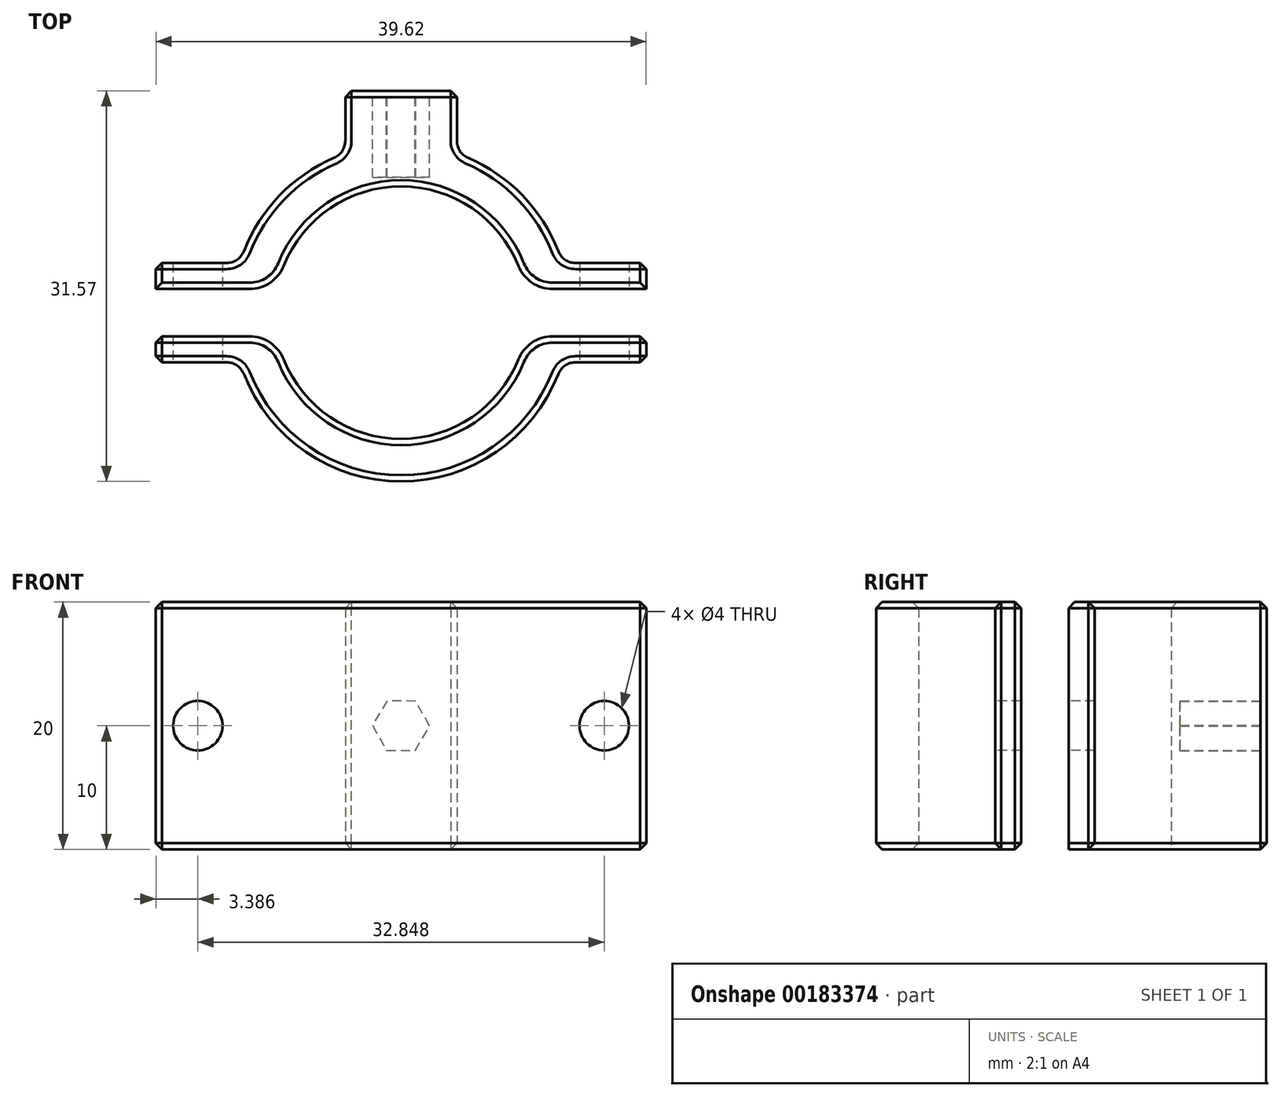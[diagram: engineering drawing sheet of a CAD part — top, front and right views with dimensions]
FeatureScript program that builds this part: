
annotation { "Feature Type Name" : "Feature", "Feature Type Description" : "" }
export const myFeature = defineFeature(function(context is Context, id is Id, definition is map)
    precondition{}
    {
        {
            var Q0;
            Q0=qCreatedBy(makeId("Top.planeOp"),FACE);
            var sketch = newSketch(context, id + "F15", { "sketchPlane" : qUnion([Q0])});
            skCircle(sketch, "E0", {"center": v(0, 0) * mm, "radius": 13.64 * mm});
            skCircle(sketch, "E1", {"center": v(0, 0) * mm, "radius": 10 * mm});
            skSolve(sketch);
        }
        {
            var Q0;
            Q0=makeQuery(id+"F15.imprint","IMPRINT",FACE,{"disambiguationData":[TD([[makeQuery(id+"F15.imprint","IMPRINT",EDGE,{"derivedFrom":sQuery(id+"F15.wireOp",EDGE,"d60e790e-70cd-4cc0-8c0c-df4997ba0fd5")}),-1.0]])]});
            var Q1;
            Q1=makeQuery(id+"F15.imprint","IMPRINT",FACE,{"disambiguationData":[TD([[makeQuery(id+"F15.imprint","IMPRINT",EDGE,{"derivedFrom":sQuery(id+"F15.wireOp",EDGE,"E0")}),1.0]])]});
            extrude(context, id + "F16", {"entities" : qUnion([Q0, Q1]), "depth" : 20 * mm});
        }
        {
            var Q0;
            Q0=qCreatedBy(makeId("Top.planeOp"),FACE);
            var sketch = newSketch(context, id + "F0", { "sketchPlane" : qUnion([Q0])});
            skLineSegment(sketch, "E2.bottom", {"start": v(19.81, 4.02) * mm, "end": v(-19.81, 4.02) * mm});
            skLineSegment(sketch, "E2.top", {"start": v(19.81, -4.02) * mm, "end": v(-19.81, -4.02) * mm});
            skLineSegment(sketch, "E2.left", {"start": v(19.81, 4.02) * mm, "end": v(19.81, -4.02) * mm});
            skLineSegment(sketch, "E2.right", {"start": v(-19.81, 4.02) * mm, "end": v(-19.81, -4.02) * mm});
            skPoint(sketch, "E2.middle", {"position": v(0, 0) * mm});
            skSolve(sketch);
        }
        {
            var Q0;
            Q0=qCreatedBy(makeId("Top.planeOp"),FACE);
            var sketch = newSketch(context, id + "F1", { "sketchPlane" : qUnion([Q0])});
            skLineSegment(sketch, "E3.bottom", {"start": v(19.81, 1.92) * mm, "end": v(-19.81, 1.92) * mm});
            skLineSegment(sketch, "E3.top", {"start": v(19.81, -1.92) * mm, "end": v(-19.81, -1.92) * mm});
            skLineSegment(sketch, "E3.left", {"start": v(19.81, 1.92) * mm, "end": v(19.81, -1.92) * mm});
            skLineSegment(sketch, "E3.right", {"start": v(-19.81, 1.92) * mm, "end": v(-19.81, -1.92) * mm});
            skPoint(sketch, "E3.middle", {"position": v(0, 0) * mm});
            skSolve(sketch);
        }
        {
            var Q0;
            Q0=makeQuery(id+"F0.imprint","IMPRINT",FACE,{"disambiguationData":[TD([[makeQuery(id+"F0.imprint","IMPRINT",EDGE,{"derivedFrom":sQuery(id+"F0.wireOp",EDGE,"E2.bottom")}),1.0]])]});
            extrude(context, id + "F17", {"entities" : qUnion([Q0]), "operationType" : NewBodyOperationType.ADD, "depth" : 20 * mm});
        }
        {
            var Q0;
            Q0=makeQuery(id+"F1.imprint","IMPRINT",FACE,{"disambiguationData":[TD([[makeQuery(id+"F1.imprint","IMPRINT",EDGE,{"derivedFrom":sQuery(id+"F1.wireOp",EDGE,"E3.bottom")}),1.0]])]});
            extrude(context, id + "F2", {"entities" : qUnion([Q0]), "operationType" : NewBodyOperationType.REMOVE, "depth" : 25 * mm});
        }
        {
            var Q0;
            Q0=qCreatedBy(makeId("Top.planeOp"),FACE);
            var sketch = newSketch(context, id + "F3", { "sketchPlane" : qUnion([Q0])});
            skCircle(sketch, "E4", {"center": v(0, 0) * mm, "radius": 10.2 * mm});
            skSolve(sketch);
        }
        {
            var Q0;
            Q0=makeQuery(id+"F3.imprint","IMPRINT",FACE,{"disambiguationData":[TD([[makeQuery(id+"F3.imprint","IMPRINT",EDGE,{"derivedFrom":sQuery(id+"F3.wireOp",EDGE,"E4")}),1.0]])]});
            extrude(context, id + "F18", {"entities" : qUnion([Q0]), "operationType" : NewBodyOperationType.REMOVE, "depth" : 25 * mm});
        }
        {
            var Q0;
            {var subQ1=sQuery(id+"F0.wireOp",EDGE,"E2.left");var subQ2=sQuery(id+"F0.wireOp",EDGE,"E2.top");Q0=makeQuery(id+"F17.boolean.opBoolean","SPLIT",FACE,{"disambiguationData":[TD([makeQuery(id+"F17.opExtrude","SWEPT_FACE",FACE,{"disambiguationData":[OSD([subQ1])]})])],"derivedFrom":makeQuery(id+"F17.opExtrude","SWEPT_FACE",FACE,{"disambiguationData":[OSD([subQ2])]})});}
            var sketch = newSketch(context, id + "F4", { "sketchPlane" : qUnion([Q0])});
            skLineSegment(sketch, "E5", {"start": v(19.81, 10) * mm, "end": v(13.03, 10) * mm, "construction": true});
            skLineSegment(sketch, "E6", {"start": v(16.42, 0) * mm, "end": v(16.42, 20) * mm, "construction": true});
            skPoint(sketch, "E7", {"position": v(16.42, 10) * mm});
            skSolve(sketch);
        }
        {
            var Q0;
            {var subQ0=sQuery(id+"F0.wireOp",EDGE,"E2.right");var subQ2=sQuery(id+"F0.wireOp",EDGE,"E2.top");Q0=makeQuery(id+"F17.boolean.opBoolean","SPLIT",FACE,{"disambiguationData":[TD([makeQuery(id+"F17.opExtrude","SWEPT_FACE",FACE,{"disambiguationData":[OSD([subQ0])]})])],"derivedFrom":makeQuery(id+"F17.opExtrude","SWEPT_FACE",FACE,{"disambiguationData":[OSD([subQ2])]})});}
            var sketch = newSketch(context, id + "F5", { "sketchPlane" : qUnion([Q0])});
            skLineSegment(sketch, "E8", {"start": v(-19.81, 10) * mm, "end": v(-13.03, 10) * mm, "construction": true});
            skLineSegment(sketch, "E9", {"start": v(-16.42, 0) * mm, "end": v(-16.42, 20) * mm, "construction": true});
            skPoint(sketch, "E10", {"position": v(-16.42, 10) * mm});
            skSolve(sketch);
        }
        {
            var Q0;
            Q0=sQuery(id+"F4.wireOp",VERTEX,"E7");
            var Q1;
            Q1=makeQuery(id+"F2.boolean.opBoolean","SPLIT",BODY,{"disambiguationData":[OD(0.0)],"derivedFrom":makeQuery(id+"F16.opExtrude","SWEPT_BODY",BODY,{"disambiguationData":[OSD([sQuery(id+"F15.wireOp",EDGE,"E0"),sQuery(id+"F15.wireOp",EDGE,"E1")])]})});
            var Q2;
            Q2=makeQuery(id+"F2.boolean.opBoolean","SPLIT",BODY,{"disambiguationData":[OD(1.0)],"derivedFrom":makeQuery(id+"F16.opExtrude","SWEPT_BODY",BODY,{"disambiguationData":[OSD([sQuery(id+"F15.wireOp",EDGE,"E0"),sQuery(id+"F15.wireOp",EDGE,"E1")])]})});
            hole(context, id + "F6", {"style" : HoleStyle.SIMPLE, "endStyle" : HoleEndStyle.THROUGH, "holeDiameter" : 4 * mm, "locations" : qUnion([Q0]), "scope" : qUnion([Q1, Q2]), "isTappedThrough" : true});
        }
        {
            var Q0;
            Q0=sQuery(id+"F5.wireOp",VERTEX,"E10");
            var Q1;
            Q1=makeQuery(id+"F2.boolean.opBoolean","SPLIT",BODY,{"disambiguationData":[OD(0.0)],"derivedFrom":makeQuery(id+"F16.opExtrude","SWEPT_BODY",BODY,{"disambiguationData":[OSD([sQuery(id+"F15.wireOp",EDGE,"E0"),sQuery(id+"F15.wireOp",EDGE,"E1")])]})});
            var Q2;
            Q2=makeQuery(id+"F2.boolean.opBoolean","SPLIT",BODY,{"disambiguationData":[OD(1.0)],"derivedFrom":makeQuery(id+"F16.opExtrude","SWEPT_BODY",BODY,{"disambiguationData":[OSD([sQuery(id+"F15.wireOp",EDGE,"E0"),sQuery(id+"F15.wireOp",EDGE,"E1")])]})});
            hole(context, id + "F7", {"style" : HoleStyle.SIMPLE, "endStyle" : HoleEndStyle.THROUGH, "holeDiameter" : 4 * mm, "locations" : qUnion([Q0]), "scope" : qUnion([Q1, Q2]), "isTappedThrough" : true});
        }
        {
            var Q0;
            Q0=qCreatedBy(makeId("Top.planeOp"),FACE);
            var sketch = newSketch(context, id + "F8", { "sketchPlane" : qUnion([Q0])});
            skLineSegment(sketch, "E11.bottom", {"start": v(4.5, 17.93) * mm, "end": v(-4.5, 17.93) * mm});
            skLineSegment(sketch, "E11.top", {"start": v(4.5, 10.7) * mm, "end": v(-4.5, 10.7) * mm});
            skLineSegment(sketch, "E11.left", {"start": v(4.5, 17.93) * mm, "end": v(4.5, 10.7) * mm});
            skLineSegment(sketch, "E11.right", {"start": v(-4.5, 17.93) * mm, "end": v(-4.5, 10.7) * mm});
            skPoint(sketch, "E11.middle", {"position": v(0, 14.31) * mm});
            skSolve(sketch);
        }
        {
            var Q0;
            Q0=makeQuery(id+"F8.imprint","IMPRINT",FACE,{"disambiguationData":[TD([[makeQuery(id+"F8.imprint","IMPRINT",EDGE,{"derivedFrom":sQuery(id+"F8.wireOp",EDGE,"E11.bottom")}),1.0]])]});
            extrude(context, id + "F9", {"entities" : qUnion([Q0]), "operationType" : NewBodyOperationType.ADD, "depth" : 20 * mm});
        }
        {
            var Q0;
            Q0=makeQuery(id+"F9.opExtrude","SWEPT_FACE",FACE,{"disambiguationData":[OSD([sQuery(id+"F8.wireOp",EDGE,"E11.bottom")])]});
            var sketch = newSketch(context, id + "F10", { "sketchPlane" : qUnion([Q0])});
            skLineSegment(sketch, "E12", {"start": v(0, 0) * mm, "end": v(0, 20) * mm, "construction": true});
            skLineSegment(sketch, "E13", {"start": v(4.5, 10) * mm, "end": v(-4.5, 10) * mm, "construction": true});
            skCircle(sketch, "E14", {"center": v(0, 10) * mm, "radius": 2 * mm});
            skCircle(sketch, "E15.cCircle", {"center": v(0, 10) * mm, "radius": 2 * mm, "construction": true});
            skLineSegment(sketch, "E15.0", {"start": v(2.3, 10.03) * mm, "end": v(1.18, 8.01) * mm});
            skLineSegment(sketch, "E15.1", {"start": v(1.18, 8.01) * mm, "end": v(-1.13, 7.99) * mm});
            skLineSegment(sketch, "E15.2", {"start": v(-1.13, 7.99) * mm, "end": v(-2.3, 9.97) * mm});
            skLineSegment(sketch, "E15.3", {"start": v(-2.3, 9.97) * mm, "end": v(-1.18, 11.99) * mm});
            skLineSegment(sketch, "E15.4", {"start": v(-1.18, 11.99) * mm, "end": v(1.13, 12.01) * mm});
            skLineSegment(sketch, "E15.5", {"start": v(1.13, 12.01) * mm, "end": v(2.3, 10.03) * mm});
            skPoint(sketch, "E15.0.midPoint", {"position": v(1.74, 9.02) * mm});
            skSolve(sketch);
        }
        {
            var Q0;
            Q0=makeQuery(id+"F17.boolean.opBoolean","INTERSECT",EDGE,{"disambiguationData":[OD(0.0)],"derivedFrom":[makeQuery(id+"F16.opExtrude","SWEPT_FACE",FACE,{"disambiguationData":[OSD([sQuery(id+"F15.wireOp",EDGE,"E0")])]}),makeQuery(id+"F17.opExtrude","SWEPT_FACE",FACE,{"disambiguationData":[OSD([sQuery(id+"F0.wireOp",EDGE,"E2.bottom")])]})]});
            var Q1;
            Q1=makeQuery(id+"F17.boolean.opBoolean","INTERSECT",EDGE,{"disambiguationData":[OD(1.0)],"derivedFrom":[makeQuery(id+"F16.opExtrude","SWEPT_FACE",FACE,{"disambiguationData":[OSD([sQuery(id+"F15.wireOp",EDGE,"E0")])]}),makeQuery(id+"F17.opExtrude","SWEPT_FACE",FACE,{"disambiguationData":[OSD([sQuery(id+"F0.wireOp",EDGE,"E2.bottom")])]})]});
            var Q2;
            {var subQ3=sQuery(id+"F0.wireOp",EDGE,"E2.bottom");var subQ5=sQuery(id+"F15.wireOp",EDGE,"E0");Q2=makeQuery(id+"F9.boolean.opBoolean","INTERSECT",EDGE,{"derivedFrom":[makeQuery(id+"F17.boolean.opBoolean","SPLIT",FACE,{"disambiguationData":[TD([makeQuery(id+"F17.opExtrude","SWEPT_FACE",FACE,{"disambiguationData":[OSD([subQ3])]})])],"derivedFrom":makeQuery(id+"F16.opExtrude","SWEPT_FACE",FACE,{"disambiguationData":[OSD([subQ5])]})}),makeQuery(id+"F9.opExtrude","SWEPT_FACE",FACE,{"disambiguationData":[OSD([sQuery(id+"F8.wireOp",EDGE,"E11.right")])]})]});}
            var Q3;
            {var subQ3=sQuery(id+"F0.wireOp",EDGE,"E2.bottom");var subQ5=sQuery(id+"F15.wireOp",EDGE,"E0");Q3=makeQuery(id+"F9.boolean.opBoolean","INTERSECT",EDGE,{"derivedFrom":[makeQuery(id+"F17.boolean.opBoolean","SPLIT",FACE,{"disambiguationData":[TD([makeQuery(id+"F17.opExtrude","SWEPT_FACE",FACE,{"disambiguationData":[OSD([subQ3])]})])],"derivedFrom":makeQuery(id+"F16.opExtrude","SWEPT_FACE",FACE,{"disambiguationData":[OSD([subQ5])]})}),makeQuery(id+"F9.opExtrude","SWEPT_FACE",FACE,{"disambiguationData":[OSD([sQuery(id+"F8.wireOp",EDGE,"E11.left")])]})]});}
            var Q4;
            Q4=makeQuery(id+"F17.boolean.opBoolean","INTERSECT",EDGE,{"disambiguationData":[OD(1.0)],"derivedFrom":[makeQuery(id+"F16.opExtrude","SWEPT_FACE",FACE,{"disambiguationData":[OSD([sQuery(id+"F15.wireOp",EDGE,"E0")])]}),makeQuery(id+"F17.opExtrude","SWEPT_FACE",FACE,{"disambiguationData":[OSD([sQuery(id+"F0.wireOp",EDGE,"E2.top")])]})]});
            var Q5;
            Q5=makeQuery(id+"F17.boolean.opBoolean","INTERSECT",EDGE,{"disambiguationData":[OD(0.0)],"derivedFrom":[makeQuery(id+"F16.opExtrude","SWEPT_FACE",FACE,{"disambiguationData":[OSD([sQuery(id+"F15.wireOp",EDGE,"E0")])]}),makeQuery(id+"F17.opExtrude","SWEPT_FACE",FACE,{"disambiguationData":[OSD([sQuery(id+"F0.wireOp",EDGE,"E2.top")])]})]});
            fillet(context, id + "F11", {"entities" : qUnion([Q0, Q1, Q2, Q3, Q4, Q5]), "radius" : 1.5 * mm, "tangentPropagation" : true, "allowEdgeOverflow" : false});
        }
        {
            var Q0;
            Q0=makeQuery(id+"F18.boolean.opBoolean","INTERSECT",EDGE,{"disambiguationData":[OD(1.0)],"derivedFrom":[makeQuery(id+"F2.boolean.opBoolean","COPY",FACE,{"derivedFrom":makeQuery(id+"F2.opExtrude","SWEPT_FACE",FACE,{"disambiguationData":[OSD([sQuery(id+"F1.wireOp",EDGE,"E3.bottom")])]})}),makeQuery(id+"F18.opExtrude","SWEPT_FACE",FACE,{"disambiguationData":[OSD([sQuery(id+"F3.wireOp",EDGE,"E4")])]})]});
            var Q1;
            Q1=makeQuery(id+"F18.boolean.opBoolean","INTERSECT",EDGE,{"disambiguationData":[OD(0.0)],"derivedFrom":[makeQuery(id+"F2.boolean.opBoolean","COPY",FACE,{"derivedFrom":makeQuery(id+"F2.opExtrude","SWEPT_FACE",FACE,{"disambiguationData":[OSD([sQuery(id+"F1.wireOp",EDGE,"E3.bottom")])]})}),makeQuery(id+"F18.opExtrude","SWEPT_FACE",FACE,{"disambiguationData":[OSD([sQuery(id+"F3.wireOp",EDGE,"E4")])]})]});
            var Q2;
            Q2=makeQuery(id+"F18.boolean.opBoolean","INTERSECT",EDGE,{"disambiguationData":[OD(1.0)],"derivedFrom":[makeQuery(id+"F2.boolean.opBoolean","COPY",FACE,{"derivedFrom":makeQuery(id+"F2.opExtrude","SWEPT_FACE",FACE,{"disambiguationData":[OSD([sQuery(id+"F1.wireOp",EDGE,"E3.top")])]})}),makeQuery(id+"F18.opExtrude","SWEPT_FACE",FACE,{"disambiguationData":[OSD([sQuery(id+"F3.wireOp",EDGE,"E4")])]})]});
            var Q3;
            Q3=makeQuery(id+"F18.boolean.opBoolean","INTERSECT",EDGE,{"disambiguationData":[OD(0.0)],"derivedFrom":[makeQuery(id+"F2.boolean.opBoolean","COPY",FACE,{"derivedFrom":makeQuery(id+"F2.opExtrude","SWEPT_FACE",FACE,{"disambiguationData":[OSD([sQuery(id+"F1.wireOp",EDGE,"E3.top")])]})}),makeQuery(id+"F18.opExtrude","SWEPT_FACE",FACE,{"disambiguationData":[OSD([sQuery(id+"F3.wireOp",EDGE,"E4")])]})]});
            fillet(context, id + "F12", {"entities" : qUnion([Q0, Q1, Q2, Q3]), "radius" : 3 * mm, "tangentPropagation" : true, "allowEdgeOverflow" : false});
        }
        {
            var Q0;
            {var subQ0=sQuery(id+"F15.wireOp",EDGE,"E0");var subQ1=sQuery(id+"F0.wireOp",EDGE,"E2.bottom");Q0=makeQuery(id+"F17.boolean.opBoolean","SPLIT",EDGE,{"disambiguationData":[TD([makeQuery(id+"F17.opExtrude","SWEPT_FACE",FACE,{"disambiguationData":[OSD([subQ1])]})])],"derivedFrom":makeQuery(id+"F16.opExtrude","CAP_EDGE",EDGE,{"disambiguationData":[OSD([subQ0])],"isStart":false})});}
            var Q1;
            {var subQ0=sQuery(id+"F15.wireOp",EDGE,"E0");var subQ1=sQuery(id+"F0.wireOp",EDGE,"E2.bottom");Q1=makeQuery(id+"F17.boolean.opBoolean","SPLIT",EDGE,{"disambiguationData":[TD([makeQuery(id+"F17.opExtrude","SWEPT_FACE",FACE,{"disambiguationData":[OSD([subQ1])]})])],"derivedFrom":makeQuery(id+"F16.opExtrude","CAP_EDGE",EDGE,{"disambiguationData":[OSD([subQ0])],"isStart":true})});}
            var Q2;
            {var subQ0=sQuery(id+"F0.wireOp",EDGE,"E2.right");var subQ1=sQuery(id+"F0.wireOp",EDGE,"E2.bottom");Q2=makeQuery(id+"F17.boolean.opBoolean","SPLIT",EDGE,{"disambiguationData":[TD([makeQuery(id+"F17.opExtrude","SWEPT_FACE",FACE,{"disambiguationData":[OSD([subQ0])]})])],"derivedFrom":makeQuery(id+"F17.opExtrude","CAP_EDGE",EDGE,{"disambiguationData":[OSD([subQ1])],"isStart":false})});}
            var Q3;
            Q3=makeQuery(id+"F17.opExtrude","SWEPT_EDGE",EDGE,{"disambiguationData":[OSD([sQuery(id+"F0.wireOp",EDGE,"E2.bottom"),sQuery(id+"F0.wireOp",EDGE,"E2.right")])]});
            var Q4;
            {var subQ0=sQuery(id+"F0.wireOp",EDGE,"E2.right");var subQ1=sQuery(id+"F0.wireOp",EDGE,"E2.bottom");Q4=makeQuery(id+"F17.boolean.opBoolean","SPLIT",EDGE,{"disambiguationData":[TD([makeQuery(id+"F17.opExtrude","SWEPT_FACE",FACE,{"disambiguationData":[OSD([subQ0])]})])],"derivedFrom":makeQuery(id+"F17.opExtrude","CAP_EDGE",EDGE,{"disambiguationData":[OSD([subQ1])],"isStart":true})});}
            var Q5;
            {var subQ0=sQuery(id+"F0.wireOp",EDGE,"E2.left");var subQ1=sQuery(id+"F0.wireOp",EDGE,"E2.bottom");Q5=makeQuery(id+"F17.boolean.opBoolean","SPLIT",EDGE,{"disambiguationData":[TD([makeQuery(id+"F17.opExtrude","SWEPT_FACE",FACE,{"disambiguationData":[OSD([subQ0])]})])],"derivedFrom":makeQuery(id+"F17.opExtrude","CAP_EDGE",EDGE,{"disambiguationData":[OSD([subQ1])],"isStart":false})});}
            var Q6;
            Q6=makeQuery(id+"F17.opExtrude","SWEPT_EDGE",EDGE,{"disambiguationData":[OSD([sQuery(id+"F0.wireOp",EDGE,"E2.bottom"),sQuery(id+"F0.wireOp",EDGE,"E2.left")])]});
            var Q7;
            {var subQ0=sQuery(id+"F0.wireOp",EDGE,"E2.left");var subQ1=sQuery(id+"F0.wireOp",EDGE,"E2.bottom");Q7=makeQuery(id+"F17.boolean.opBoolean","SPLIT",EDGE,{"disambiguationData":[TD([makeQuery(id+"F17.opExtrude","SWEPT_FACE",FACE,{"disambiguationData":[OSD([subQ0])]})])],"derivedFrom":makeQuery(id+"F17.opExtrude","CAP_EDGE",EDGE,{"disambiguationData":[OSD([subQ1])],"isStart":true})});}
            var Q8;
            Q8=makeQuery(id+"F9.opExtrude","CAP_EDGE",EDGE,{"disambiguationData":[OSD([sQuery(id+"F8.wireOp",EDGE,"E11.bottom")])],"isStart":false});
            var Q9;
            Q9=makeQuery(id+"F9.opExtrude","CAP_EDGE",EDGE,{"disambiguationData":[OSD([sQuery(id+"F8.wireOp",EDGE,"E11.right")])],"isStart":false});
            var Q10;
            Q10=makeQuery(id+"F9.opExtrude","CAP_EDGE",EDGE,{"disambiguationData":[OSD([sQuery(id+"F8.wireOp",EDGE,"E11.left")])],"isStart":false});
            var Q11;
            Q11=makeQuery(id+"F9.opExtrude","CAP_EDGE",EDGE,{"disambiguationData":[OSD([sQuery(id+"F8.wireOp",EDGE,"E11.bottom")])],"isStart":true});
            var Q12;
            Q12=makeQuery(id+"F9.opExtrude","CAP_EDGE",EDGE,{"disambiguationData":[OSD([sQuery(id+"F8.wireOp",EDGE,"E11.right")])],"isStart":true});
            var Q13;
            Q13=makeQuery(id+"F9.opExtrude","SWEPT_EDGE",EDGE,{"disambiguationData":[OSD([sQuery(id+"F8.wireOp",EDGE,"E11.bottom"),sQuery(id+"F8.wireOp",EDGE,"E11.right")])]});
            var Q14;
            Q14=makeQuery(id+"F9.opExtrude","SWEPT_EDGE",EDGE,{"disambiguationData":[OSD([sQuery(id+"F8.wireOp",EDGE,"E11.bottom"),sQuery(id+"F8.wireOp",EDGE,"E11.left")])]});
            var Q15;
            Q15=makeQuery(id+"F9.opExtrude","CAP_EDGE",EDGE,{"disambiguationData":[OSD([sQuery(id+"F8.wireOp",EDGE,"E11.left")])],"isStart":true});
            var Q16;
            {var subQ0=sQuery(id+"F0.wireOp",EDGE,"E2.right");var subQ1=sQuery(id+"F0.wireOp",EDGE,"E2.bottom");Q16=makeQuery(id+"F2.boolean.opBoolean","SPLIT",EDGE,{"disambiguationData":[TD([makeQuery(id+"F17.opExtrude","SWEPT_FACE",FACE,{"disambiguationData":[OSD([subQ1])]})])],"derivedFrom":makeQuery(id+"F17.opExtrude","CAP_EDGE",EDGE,{"disambiguationData":[OSD([subQ0])],"isStart":true})});}
            var Q17;
            {var subQ0=sQuery(id+"F1.wireOp",EDGE,"E3.bottom");var subQ1=sQuery(id+"F0.wireOp",EDGE,"E2.right");Q17=makeQuery(id+"F18.boolean.opBoolean","SPLIT",EDGE,{"disambiguationData":[TD([makeQuery(id+"F17.opExtrude","SWEPT_FACE",FACE,{"disambiguationData":[OSD([subQ1])]})])],"derivedFrom":makeQuery(id+"F2.boolean.opBoolean","COPY",EDGE,{"derivedFrom":makeQuery(id+"F2.opExtrude","CAP_EDGE",EDGE,{"disambiguationData":[OSD([subQ0])],"isStart":true})})});}
            var Q18;
            Q18=makeQuery(id+"F2.boolean.opBoolean","INTERSECT",EDGE,{"derivedFrom":[makeQuery(id+"F17.opExtrude","SWEPT_FACE",FACE,{"disambiguationData":[OSD([sQuery(id+"F0.wireOp",EDGE,"E2.right")])]}),makeQuery(id+"F2.opExtrude","SWEPT_FACE",FACE,{"disambiguationData":[OSD([sQuery(id+"F1.wireOp",EDGE,"E3.bottom")])]})]});
            var Q19;
            {var subQ0=sQuery(id+"F0.wireOp",EDGE,"E2.right");var subQ1=sQuery(id+"F0.wireOp",EDGE,"E2.bottom");Q19=makeQuery(id+"F2.boolean.opBoolean","SPLIT",EDGE,{"disambiguationData":[TD([makeQuery(id+"F17.opExtrude","SWEPT_FACE",FACE,{"disambiguationData":[OSD([subQ1])]})])],"derivedFrom":makeQuery(id+"F17.opExtrude","CAP_EDGE",EDGE,{"disambiguationData":[OSD([subQ0])],"isStart":false})});}
            var Q20;
            {var subQ0=makeQuery(id+"F2.opExtrude","SWEPT_FACE",FACE,{"disambiguationData":[OSD([sQuery(id+"F1.wireOp",EDGE,"E3.bottom")])]});var subQ1=sQuery(id+"F0.wireOp",EDGE,"E2.right");var subQ2=makeQuery(id+"F17.opExtrude","CAP_FACE",FACE,{"disambiguationData":[OSD([sQuery(id+"F0.wireOp",EDGE,"E2.bottom"),sQuery(id+"F0.wireOp",EDGE,"E2.top"),sQuery(id+"F0.wireOp",EDGE,"E2.left"),subQ1])],"isStart":false});var subQ3=makeQuery(id+"F16.opExtrude","CAP_FACE",FACE,{"disambiguationData":[OSD([sQuery(id+"F15.wireOp",EDGE,"E0"),sQuery(id+"F15.wireOp",EDGE,"E1")])],"isStart":false});Q20=makeQuery(id+"F18.boolean.opBoolean","SPLIT",EDGE,{"disambiguationData":[TD([makeQuery(id+"F17.opExtrude","SWEPT_FACE",FACE,{"disambiguationData":[OSD([subQ1])]})])],"derivedFrom":makeQuery(id+"F2.boolean.opBoolean","INTERSECT",EDGE,{"derivedFrom":[makeQuery(id+"F17.boolean.opBoolean","MERGE",FACE,{"derivedFrom":[subQ3,subQ2]}),subQ0]})});}
            var Q21;
            {var subQ0=makeQuery(id+"F2.opExtrude","SWEPT_FACE",FACE,{"disambiguationData":[OSD([sQuery(id+"F1.wireOp",EDGE,"E3.top")])]});var subQ1=sQuery(id+"F0.wireOp",EDGE,"E2.right");var subQ2=makeQuery(id+"F17.opExtrude","CAP_FACE",FACE,{"disambiguationData":[OSD([sQuery(id+"F0.wireOp",EDGE,"E2.bottom"),sQuery(id+"F0.wireOp",EDGE,"E2.top"),sQuery(id+"F0.wireOp",EDGE,"E2.left"),subQ1])],"isStart":false});var subQ3=makeQuery(id+"F16.opExtrude","CAP_FACE",FACE,{"disambiguationData":[OSD([sQuery(id+"F15.wireOp",EDGE,"E0"),sQuery(id+"F15.wireOp",EDGE,"E1")])],"isStart":false});Q21=makeQuery(id+"F18.boolean.opBoolean","SPLIT",EDGE,{"disambiguationData":[TD([makeQuery(id+"F17.opExtrude","SWEPT_FACE",FACE,{"disambiguationData":[OSD([subQ1])]})])],"derivedFrom":makeQuery(id+"F2.boolean.opBoolean","INTERSECT",EDGE,{"derivedFrom":[makeQuery(id+"F17.boolean.opBoolean","MERGE",FACE,{"derivedFrom":[subQ3,subQ2]}),subQ0]})});}
            var Q22;
            {var subQ0=sQuery(id+"F0.wireOp",EDGE,"E2.top");var subQ1=sQuery(id+"F0.wireOp",EDGE,"E2.right");Q22=makeQuery(id+"F17.boolean.opBoolean","SPLIT",EDGE,{"disambiguationData":[TD([makeQuery(id+"F17.opExtrude","SWEPT_FACE",FACE,{"disambiguationData":[OSD([subQ1])]})])],"derivedFrom":makeQuery(id+"F17.opExtrude","CAP_EDGE",EDGE,{"disambiguationData":[OSD([subQ0])],"isStart":false})});}
            var Q23;
            {var subQ0=sQuery(id+"F0.wireOp",EDGE,"E2.right");var subQ1=sQuery(id+"F0.wireOp",EDGE,"E2.top");Q23=makeQuery(id+"F2.boolean.opBoolean","SPLIT",EDGE,{"disambiguationData":[TD([makeQuery(id+"F17.opExtrude","SWEPT_FACE",FACE,{"disambiguationData":[OSD([subQ1])]})])],"derivedFrom":makeQuery(id+"F17.opExtrude","CAP_EDGE",EDGE,{"disambiguationData":[OSD([subQ0])],"isStart":false})});}
            var Q24;
            Q24=makeQuery(id+"F17.opExtrude","SWEPT_EDGE",EDGE,{"disambiguationData":[OSD([sQuery(id+"F0.wireOp",EDGE,"E2.top"),sQuery(id+"F0.wireOp",EDGE,"E2.right")])]});
            var Q25;
            Q25=makeQuery(id+"F2.boolean.opBoolean","INTERSECT",EDGE,{"derivedFrom":[makeQuery(id+"F17.opExtrude","SWEPT_FACE",FACE,{"disambiguationData":[OSD([sQuery(id+"F0.wireOp",EDGE,"E2.right")])]}),makeQuery(id+"F2.opExtrude","SWEPT_FACE",FACE,{"disambiguationData":[OSD([sQuery(id+"F1.wireOp",EDGE,"E3.top")])]})]});
            var Q26;
            {var subQ0=sQuery(id+"F0.wireOp",EDGE,"E2.top");var subQ1=sQuery(id+"F0.wireOp",EDGE,"E2.right");Q26=makeQuery(id+"F17.boolean.opBoolean","SPLIT",EDGE,{"disambiguationData":[TD([makeQuery(id+"F17.opExtrude","SWEPT_FACE",FACE,{"disambiguationData":[OSD([subQ1])]})])],"derivedFrom":makeQuery(id+"F17.opExtrude","CAP_EDGE",EDGE,{"disambiguationData":[OSD([subQ0])],"isStart":true})});}
            var Q27;
            {var subQ0=sQuery(id+"F1.wireOp",EDGE,"E3.top");var subQ1=sQuery(id+"F0.wireOp",EDGE,"E2.right");Q27=makeQuery(id+"F18.boolean.opBoolean","SPLIT",EDGE,{"disambiguationData":[TD([makeQuery(id+"F17.opExtrude","SWEPT_FACE",FACE,{"disambiguationData":[OSD([subQ1])]})])],"derivedFrom":makeQuery(id+"F2.boolean.opBoolean","COPY",EDGE,{"derivedFrom":makeQuery(id+"F2.opExtrude","CAP_EDGE",EDGE,{"disambiguationData":[OSD([subQ0])],"isStart":true})})});}
            var Q28;
            {var subQ0=sQuery(id+"F0.wireOp",EDGE,"E2.top");var subQ1=sQuery(id+"F0.wireOp",EDGE,"E2.right");Q28=makeQuery(id+"F2.boolean.opBoolean","SPLIT",EDGE,{"disambiguationData":[TD([makeQuery(id+"F17.opExtrude","SWEPT_FACE",FACE,{"disambiguationData":[OSD([subQ0])]})])],"derivedFrom":makeQuery(id+"F17.opExtrude","CAP_EDGE",EDGE,{"disambiguationData":[OSD([subQ1])],"isStart":true})});}
            var Q29;
            {var subQ0=sQuery(id+"F15.wireOp",EDGE,"E0");var subQ1=sQuery(id+"F0.wireOp",EDGE,"E2.top");Q29=makeQuery(id+"F17.boolean.opBoolean","SPLIT",EDGE,{"disambiguationData":[TD([makeQuery(id+"F17.opExtrude","SWEPT_FACE",FACE,{"disambiguationData":[OSD([subQ1])]})])],"derivedFrom":makeQuery(id+"F16.opExtrude","CAP_EDGE",EDGE,{"disambiguationData":[OSD([subQ0])],"isStart":true})});}
            var Q30;
            {var subQ0=sQuery(id+"F15.wireOp",EDGE,"E0");var subQ1=sQuery(id+"F0.wireOp",EDGE,"E2.top");Q30=makeQuery(id+"F17.boolean.opBoolean","SPLIT",EDGE,{"disambiguationData":[TD([makeQuery(id+"F17.opExtrude","SWEPT_FACE",FACE,{"disambiguationData":[OSD([subQ1])]})])],"derivedFrom":makeQuery(id+"F16.opExtrude","CAP_EDGE",EDGE,{"disambiguationData":[OSD([subQ0])],"isStart":false})});}
            var Q31;
            {var subQ0=sQuery(id+"F0.wireOp",EDGE,"E2.top");var subQ1=sQuery(id+"F0.wireOp",EDGE,"E2.left");Q31=makeQuery(id+"F17.boolean.opBoolean","SPLIT",EDGE,{"disambiguationData":[TD([makeQuery(id+"F17.opExtrude","SWEPT_FACE",FACE,{"disambiguationData":[OSD([subQ1])]})])],"derivedFrom":makeQuery(id+"F17.opExtrude","CAP_EDGE",EDGE,{"disambiguationData":[OSD([subQ0])],"isStart":true})});}
            var Q32;
            {var subQ0=sQuery(id+"F0.wireOp",EDGE,"E2.top");var subQ1=sQuery(id+"F0.wireOp",EDGE,"E2.left");Q32=makeQuery(id+"F17.boolean.opBoolean","SPLIT",EDGE,{"disambiguationData":[TD([makeQuery(id+"F17.opExtrude","SWEPT_FACE",FACE,{"disambiguationData":[OSD([subQ1])]})])],"derivedFrom":makeQuery(id+"F17.opExtrude","CAP_EDGE",EDGE,{"disambiguationData":[OSD([subQ0])],"isStart":false})});}
            var Q33;
            Q33=makeQuery(id+"F17.opExtrude","SWEPT_EDGE",EDGE,{"disambiguationData":[OSD([sQuery(id+"F0.wireOp",EDGE,"E2.top"),sQuery(id+"F0.wireOp",EDGE,"E2.left")])]});
            var Q34;
            Q34=makeQuery(id+"F2.boolean.opBoolean","INTERSECT",EDGE,{"derivedFrom":[makeQuery(id+"F17.opExtrude","SWEPT_FACE",FACE,{"disambiguationData":[OSD([sQuery(id+"F0.wireOp",EDGE,"E2.left")])]}),makeQuery(id+"F2.opExtrude","SWEPT_FACE",FACE,{"disambiguationData":[OSD([sQuery(id+"F1.wireOp",EDGE,"E3.top")])]})]});
            var Q35;
            {var subQ0=sQuery(id+"F0.wireOp",EDGE,"E2.left");var subQ1=sQuery(id+"F0.wireOp",EDGE,"E2.top");Q35=makeQuery(id+"F2.boolean.opBoolean","SPLIT",EDGE,{"disambiguationData":[TD([makeQuery(id+"F17.opExtrude","SWEPT_FACE",FACE,{"disambiguationData":[OSD([subQ1])]})])],"derivedFrom":makeQuery(id+"F17.opExtrude","CAP_EDGE",EDGE,{"disambiguationData":[OSD([subQ0])],"isStart":false})});}
            var Q36;
            {var subQ0=makeQuery(id+"F2.opExtrude","SWEPT_FACE",FACE,{"disambiguationData":[OSD([sQuery(id+"F1.wireOp",EDGE,"E3.top")])]});var subQ1=sQuery(id+"F0.wireOp",EDGE,"E2.left");var subQ2=makeQuery(id+"F17.opExtrude","CAP_FACE",FACE,{"disambiguationData":[OSD([sQuery(id+"F0.wireOp",EDGE,"E2.bottom"),sQuery(id+"F0.wireOp",EDGE,"E2.top"),subQ1,sQuery(id+"F0.wireOp",EDGE,"E2.right")])],"isStart":false});var subQ3=makeQuery(id+"F16.opExtrude","CAP_FACE",FACE,{"disambiguationData":[OSD([sQuery(id+"F15.wireOp",EDGE,"E0"),sQuery(id+"F15.wireOp",EDGE,"E1")])],"isStart":false});Q36=makeQuery(id+"F18.boolean.opBoolean","SPLIT",EDGE,{"disambiguationData":[TD([makeQuery(id+"F17.opExtrude","SWEPT_FACE",FACE,{"disambiguationData":[OSD([subQ1])]})])],"derivedFrom":makeQuery(id+"F2.boolean.opBoolean","INTERSECT",EDGE,{"derivedFrom":[makeQuery(id+"F17.boolean.opBoolean","MERGE",FACE,{"derivedFrom":[subQ3,subQ2]}),subQ0]})});}
            var Q37;
            Q37=makeQuery(id+"F2.boolean.opBoolean","INTERSECT",EDGE,{"derivedFrom":[makeQuery(id+"F17.opExtrude","SWEPT_FACE",FACE,{"disambiguationData":[OSD([sQuery(id+"F0.wireOp",EDGE,"E2.left")])]}),makeQuery(id+"F2.opExtrude","SWEPT_FACE",FACE,{"disambiguationData":[OSD([sQuery(id+"F1.wireOp",EDGE,"E3.bottom")])]})]});
            var Q38;
            {var subQ0=sQuery(id+"F0.wireOp",EDGE,"E2.left");var subQ1=sQuery(id+"F0.wireOp",EDGE,"E2.bottom");Q38=makeQuery(id+"F2.boolean.opBoolean","SPLIT",EDGE,{"disambiguationData":[TD([makeQuery(id+"F17.opExtrude","SWEPT_FACE",FACE,{"disambiguationData":[OSD([subQ1])]})])],"derivedFrom":makeQuery(id+"F17.opExtrude","CAP_EDGE",EDGE,{"disambiguationData":[OSD([subQ0])],"isStart":false})});}
            var Q39;
            {var subQ0=makeQuery(id+"F2.opExtrude","SWEPT_FACE",FACE,{"disambiguationData":[OSD([sQuery(id+"F1.wireOp",EDGE,"E3.bottom")])]});var subQ1=sQuery(id+"F0.wireOp",EDGE,"E2.left");var subQ2=makeQuery(id+"F17.opExtrude","CAP_FACE",FACE,{"disambiguationData":[OSD([sQuery(id+"F0.wireOp",EDGE,"E2.bottom"),sQuery(id+"F0.wireOp",EDGE,"E2.top"),subQ1,sQuery(id+"F0.wireOp",EDGE,"E2.right")])],"isStart":false});var subQ3=makeQuery(id+"F16.opExtrude","CAP_FACE",FACE,{"disambiguationData":[OSD([sQuery(id+"F15.wireOp",EDGE,"E0"),sQuery(id+"F15.wireOp",EDGE,"E1")])],"isStart":false});Q39=makeQuery(id+"F18.boolean.opBoolean","SPLIT",EDGE,{"disambiguationData":[TD([makeQuery(id+"F17.opExtrude","SWEPT_FACE",FACE,{"disambiguationData":[OSD([subQ1])]})])],"derivedFrom":makeQuery(id+"F2.boolean.opBoolean","INTERSECT",EDGE,{"derivedFrom":[makeQuery(id+"F17.boolean.opBoolean","MERGE",FACE,{"derivedFrom":[subQ3,subQ2]}),subQ0]})});}
            var Q40;
            {var subQ0=sQuery(id+"F0.wireOp",EDGE,"E2.left");var subQ1=sQuery(id+"F0.wireOp",EDGE,"E2.bottom");Q40=makeQuery(id+"F2.boolean.opBoolean","SPLIT",EDGE,{"disambiguationData":[TD([makeQuery(id+"F17.opExtrude","SWEPT_FACE",FACE,{"disambiguationData":[OSD([subQ1])]})])],"derivedFrom":makeQuery(id+"F17.opExtrude","CAP_EDGE",EDGE,{"disambiguationData":[OSD([subQ0])],"isStart":true})});}
            var Q41;
            {var subQ0=sQuery(id+"F0.wireOp",EDGE,"E2.top");var subQ1=sQuery(id+"F0.wireOp",EDGE,"E2.left");Q41=makeQuery(id+"F2.boolean.opBoolean","SPLIT",EDGE,{"disambiguationData":[TD([makeQuery(id+"F17.opExtrude","SWEPT_FACE",FACE,{"disambiguationData":[OSD([subQ0])]})])],"derivedFrom":makeQuery(id+"F17.opExtrude","CAP_EDGE",EDGE,{"disambiguationData":[OSD([subQ1])],"isStart":true})});}
            var Q42;
            {var subQ0=sQuery(id+"F1.wireOp",EDGE,"E3.bottom");var subQ1=sQuery(id+"F0.wireOp",EDGE,"E2.left");Q42=makeQuery(id+"F18.boolean.opBoolean","SPLIT",EDGE,{"disambiguationData":[TD([makeQuery(id+"F17.opExtrude","SWEPT_FACE",FACE,{"disambiguationData":[OSD([subQ1])]})])],"derivedFrom":makeQuery(id+"F2.boolean.opBoolean","COPY",EDGE,{"derivedFrom":makeQuery(id+"F2.opExtrude","CAP_EDGE",EDGE,{"disambiguationData":[OSD([subQ0])],"isStart":true})})});}
            var Q43;
            {var subQ0=sQuery(id+"F1.wireOp",EDGE,"E3.top");var subQ1=sQuery(id+"F0.wireOp",EDGE,"E2.left");Q43=makeQuery(id+"F18.boolean.opBoolean","SPLIT",EDGE,{"disambiguationData":[TD([makeQuery(id+"F17.opExtrude","SWEPT_FACE",FACE,{"disambiguationData":[OSD([subQ1])]})])],"derivedFrom":makeQuery(id+"F2.boolean.opBoolean","COPY",EDGE,{"derivedFrom":makeQuery(id+"F2.opExtrude","CAP_EDGE",EDGE,{"disambiguationData":[OSD([subQ0])],"isStart":true})})});}
            chamfer(context, id + "F13", {"entities" : qUnion([Q0, Q1, Q2, Q3, Q4, Q5, Q6, Q7, Q8, Q9, Q10, Q11, Q12, Q13, Q14, Q15, Q16, Q17, Q18, Q19, Q20, Q21, Q22, Q23, Q24, Q25, Q26, Q27, Q28, Q29, Q30, Q31, Q32, Q33, Q34, Q35, Q36, Q37, Q38, Q39, Q40, Q41, Q42, Q43]), "width" : 0.5 * mm, "tangentPropagation" : true});
        }
        {
            var Q0;
            {var subQ0=sQuery(id+"F10.wireOp",EDGE,"E14");var subQ4=makeQuery(id+"F10.imprint","INTERSECT",VERTEX,{"derivedFrom":[subQ0,sQuery(id+"F10.wireOp",EDGE,"E15.4")]});Q0=makeQuery(id+"F10.imprint","IMPRINT",FACE,{"disambiguationData":[TD([[makeQuery(id+"F10.imprint","IMPRINT",EDGE,{"disambiguationData":[TD([[subQ4,1.0]])],"derivedFrom":subQ0}),1.0]])]});}
            var Q1;
            {var subQ0=sQuery(id+"F10.wireOp",EDGE,"E15.4");var subQ1=sQuery(id+"F10.wireOp",EDGE,"E14");var subQ2=makeQuery(id+"F10.imprint","INTERSECT",VERTEX,{"derivedFrom":[subQ1,subQ0]});Q1=makeQuery(id+"F10.imprint","IMPRINT",FACE,{"disambiguationData":[TD([[makeQuery(id+"F10.imprint","IMPRINT",EDGE,{"disambiguationData":[TD([[subQ2,1.0]])],"derivedFrom":subQ1}),-1.0]])]});}
            var Q2;
            {var subQ0=sQuery(id+"F10.wireOp",EDGE,"E15.5");var subQ1=sQuery(id+"F10.wireOp",EDGE,"E14");var subQ2=makeQuery(id+"F10.imprint","INTERSECT",VERTEX,{"derivedFrom":[subQ1,subQ0]});Q2=makeQuery(id+"F10.imprint","IMPRINT",FACE,{"disambiguationData":[TD([[makeQuery(id+"F10.imprint","IMPRINT",EDGE,{"disambiguationData":[TD([[subQ2,1.0]])],"derivedFrom":subQ1}),-1.0]])]});}
            var Q3;
            {var subQ0=sQuery(id+"F10.wireOp",EDGE,"E15.1");var subQ1=sQuery(id+"F10.wireOp",EDGE,"E14");var subQ2=makeQuery(id+"F10.imprint","INTERSECT",VERTEX,{"derivedFrom":[subQ1,subQ0]});Q3=makeQuery(id+"F10.imprint","IMPRINT",FACE,{"disambiguationData":[TD([[makeQuery(id+"F10.imprint","IMPRINT",EDGE,{"disambiguationData":[TD([[subQ2,-1.0]])],"derivedFrom":subQ1}),-1.0]])]});}
            var Q4;
            {var subQ0=sQuery(id+"F10.wireOp",EDGE,"E15.2");var subQ1=sQuery(id+"F10.wireOp",EDGE,"E14");var subQ2=makeQuery(id+"F10.imprint","INTERSECT",VERTEX,{"derivedFrom":[subQ1,subQ0]});Q4=makeQuery(id+"F10.imprint","IMPRINT",FACE,{"disambiguationData":[TD([[makeQuery(id+"F10.imprint","IMPRINT",EDGE,{"disambiguationData":[TD([[subQ2,-1.0]])],"derivedFrom":subQ1}),-1.0]])]});}
            var Q5;
            {var subQ0=sQuery(id+"F10.wireOp",EDGE,"E15.3");var subQ1=sQuery(id+"F10.wireOp",EDGE,"E14");var subQ2=makeQuery(id+"F10.imprint","INTERSECT",VERTEX,{"derivedFrom":[subQ1,subQ0]});Q5=makeQuery(id+"F10.imprint","IMPRINT",FACE,{"disambiguationData":[TD([[makeQuery(id+"F10.imprint","IMPRINT",EDGE,{"disambiguationData":[TD([[subQ2,-1.0]])],"derivedFrom":subQ1}),-1.0]])]});}
            var Q6;
            {var subQ0=sQuery(id+"F10.wireOp",EDGE,"E15.4");var subQ1=sQuery(id+"F10.wireOp",EDGE,"E14");var subQ2=makeQuery(id+"F10.imprint","INTERSECT",VERTEX,{"derivedFrom":[subQ1,subQ0]});Q6=makeQuery(id+"F10.imprint","IMPRINT",FACE,{"disambiguationData":[TD([[makeQuery(id+"F10.imprint","IMPRINT",EDGE,{"disambiguationData":[TD([[subQ2,-1.0]])],"derivedFrom":subQ1}),-1.0]])]});}
            extrude(context, id + "F14", {"entities" : qUnion([Q0, Q1, Q2, Q3, Q4, Q5, Q6]), "operationType" : NewBodyOperationType.REMOVE, "oppositeDirection" : true, "depth" : 7 * mm});
        }
    });
